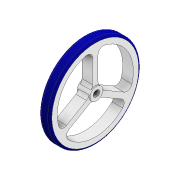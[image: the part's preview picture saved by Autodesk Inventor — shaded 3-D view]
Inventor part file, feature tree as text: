
AUTODESK INVENTOR PART (.ipt)
format: ipt  version: 2022 (Build 260153000, 153)  size: 190,464 bytes
history: native  units: mm
features: extrude x4, sketch x4, fillet x2, projected_geometry x1
ambient origin geometry x8: Origin, YZ Plane, XZ Plane, XY Plane, X Axis, Y Axis, Z Axis, Center Point
bodies: Solid1 (feature_tree)
feature tree (11):
  extrude  "Extrusion1"  Depth=10.0mm TaperAngle=0.0deg
  fillet  "Fillet1"  Radius=2.0mm
  extrude  "Extrusion2"  Depth=12.0mm TaperAngle=0.0deg
  extrude  "Extrusion3"  Depth=3.0mm
  extrude  "Extrusion4"  Depth=5.0mm
  fillet  "Fillet2"  Radius=5.0mm
  sketch  "Sketch1"  dims[d0=85.5mm d1=10.0mm d2=0.0mm d3=2.0mm]
  sketch  "Sketch2"  dims[d9=12.0mm d10=12.0mm d11=0.0mm]
  sketch  "Sketch3"  dims[d12=3.0mm d13=2.5mm]
  sketch  "Sketch4"  dims[d14=0.0mm d15=0.0mm d17=71.5mm d18=5.0mm d19=30.0mm d21=360.0deg d23=0.0mm d24=0.0mm d25=5.0mm]
  projected_geometry  "Project Cut Edges1"
